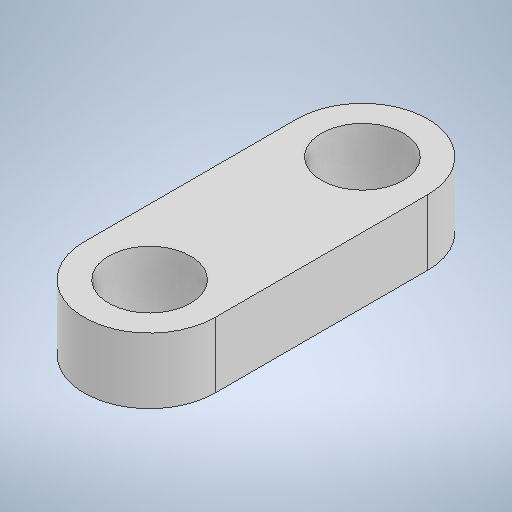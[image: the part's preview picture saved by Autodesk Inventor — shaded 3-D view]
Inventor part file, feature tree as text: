
AUTODESK INVENTOR PART (.ipt)
format: ipt  version: 2025.1 (Build 291241000, 241)  size: 226,816 bytes
history: native  units: mm
features: sketch x2, extrude x1, hole x1
ambient origin geometry x8: Origin, YZ Plane, XZ Plane, XY Plane, X Axis, Y Axis, Z Axis, Center Point
bodies: Solid1 (feature_tree)
feature tree (4):
  extrude  "Extrusion1"  Depth=8.0mm
  hole  "Hole1"  [1 undecoded]
  sketch  "Sketch1"  dims[d0=13.0mm d1=8.0mm]
  sketch  "Sketch2"  dims[d2=4.0mm d3=0.0mm d4=5.0mm d5=6.0mm d6=4.0mm d7=2.0mm d8=90.0deg d9=8.0mm d10=0.0mm]
note: 1 required parameter value undecoded (feature->parameter linkage not recoverable at this tier; creation-order binding heuristic only, values carry confidence <= 0.55)
